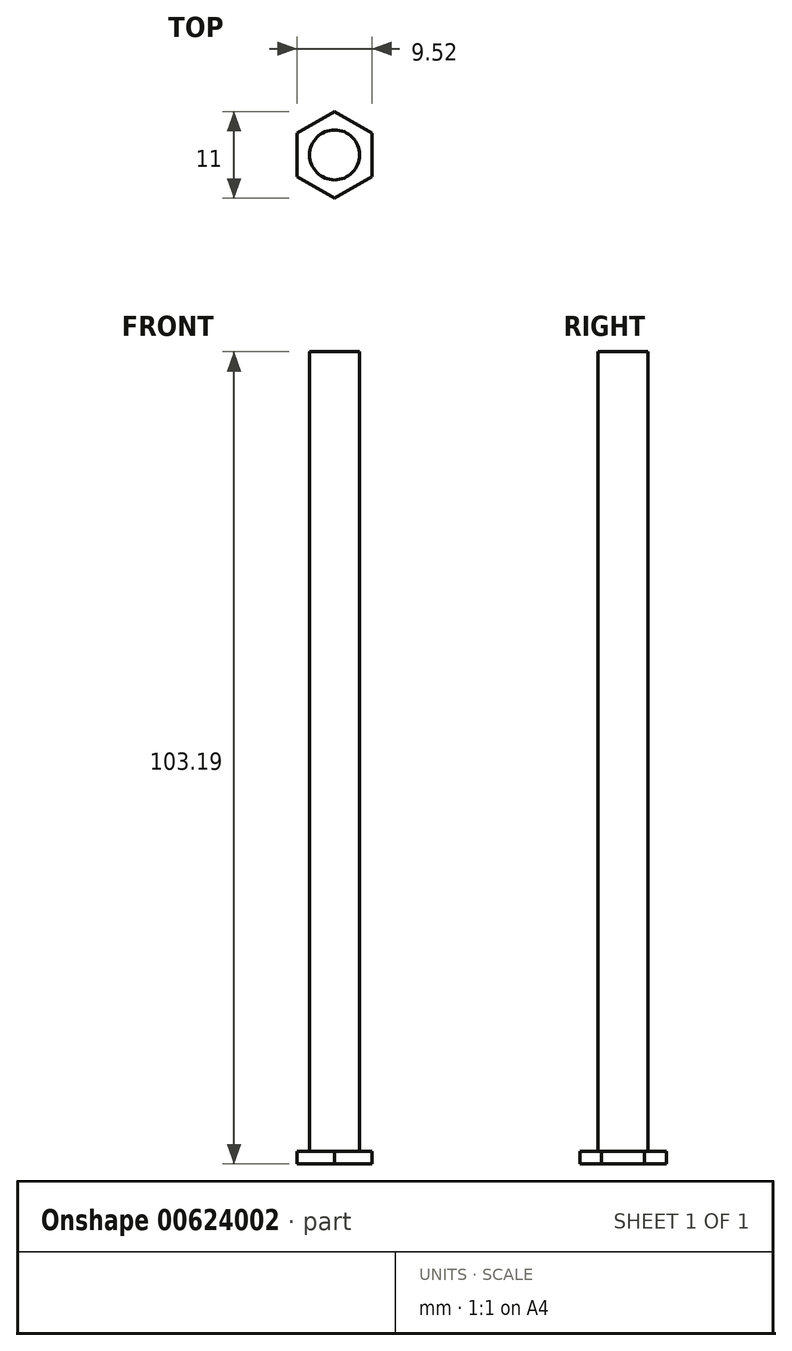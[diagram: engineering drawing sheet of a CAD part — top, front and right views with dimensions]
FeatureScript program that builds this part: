
annotation { "Feature Type Name" : "Feature", "Feature Type Description" : "" }
export const myFeature = defineFeature(function(context is Context, id is Id, definition is map)
    precondition{}
    {
        {
            var Q0;
            Q0=qCreatedBy(makeId("Top.planeOp"),FACE);
            var sketch = newSketch(context, id + "F0", { "sketchPlane" : qUnion([Q0])});
            skCircle(sketch, "E0.cCircle", {"center": v(0, 0) * mm, "radius": 4.76 * mm, "construction": true});
            skLineSegment(sketch, "E0.0", {"start": v(4.76, 2.75) * mm, "end": v(4.76, -2.75) * mm});
            skLineSegment(sketch, "E0.1", {"start": v(4.76, -2.75) * mm, "end": v(0, -5.5) * mm});
            skLineSegment(sketch, "E0.2", {"start": v(0, -5.5) * mm, "end": v(-4.76, -2.75) * mm});
            skLineSegment(sketch, "E0.3", {"start": v(-4.76, -2.75) * mm, "end": v(-4.76, 2.75) * mm});
            skLineSegment(sketch, "E0.4", {"start": v(-4.76, 2.75) * mm, "end": v(0, 5.5) * mm});
            skLineSegment(sketch, "E0.5", {"start": v(0, 5.5) * mm, "end": v(4.76, 2.75) * mm});
            skPoint(sketch, "E0.0.midPoint", {"position": v(4.76, 0) * mm});
            skSolve(sketch);
        }
        {
            var Q0;
            Q0=makeQuery(id+"F0.imprint","IMPRINT",FACE,{"disambiguationData":[TD([[makeQuery(id+"F0.imprint","IMPRINT",EDGE,{"derivedFrom":sQuery(id+"F0.wireOp",EDGE,"E0.0")}),-1.0]])]});
            extrude(context, id + "F1", {"entities" : qUnion([Q0]), "depth" : 1.59 * mm, "offsetDistance" : 25.4 * mm});
        }
        {
            var Q0;
            Q0=makeQuery(id+"F1.opExtrude","CAP_FACE",FACE,{"disambiguationData":[OSD([sQuery(id+"F0.wireOp",EDGE,"E0.0"),sQuery(id+"F0.wireOp",EDGE,"E0.1"),sQuery(id+"F0.wireOp",EDGE,"E0.2"),sQuery(id+"F0.wireOp",EDGE,"E0.3"),sQuery(id+"F0.wireOp",EDGE,"E0.4"),sQuery(id+"F0.wireOp",EDGE,"E0.5")])],"isStart":false});
            var sketch = newSketch(context, id + "F2", { "sketchPlane" : qUnion([Q0])});
            skCircle(sketch, "E1", {"center": v(0, 0) * mm, "radius": 3.18 * mm});
            skPoint(sketch, "E1.centerSnap0", {"position": v(-4.76, 0) * mm});
            skSolve(sketch);
        }
        {
            var Q0;
            Q0=makeQuery(id+"F2.imprint","IMPRINT",FACE,{"disambiguationData":[TD([[makeQuery(id+"F2.imprint","IMPRINT",EDGE,{"derivedFrom":sQuery(id+"F2.wireOp",EDGE,"E1")}),1.0]])]});
            extrude(context, id + "F3", {"entities" : qUnion([Q0]), "operationType" : NewBodyOperationType.ADD, "depth" : 101.6 * mm, "offsetDistance" : 25.4 * mm});
        }
    });
